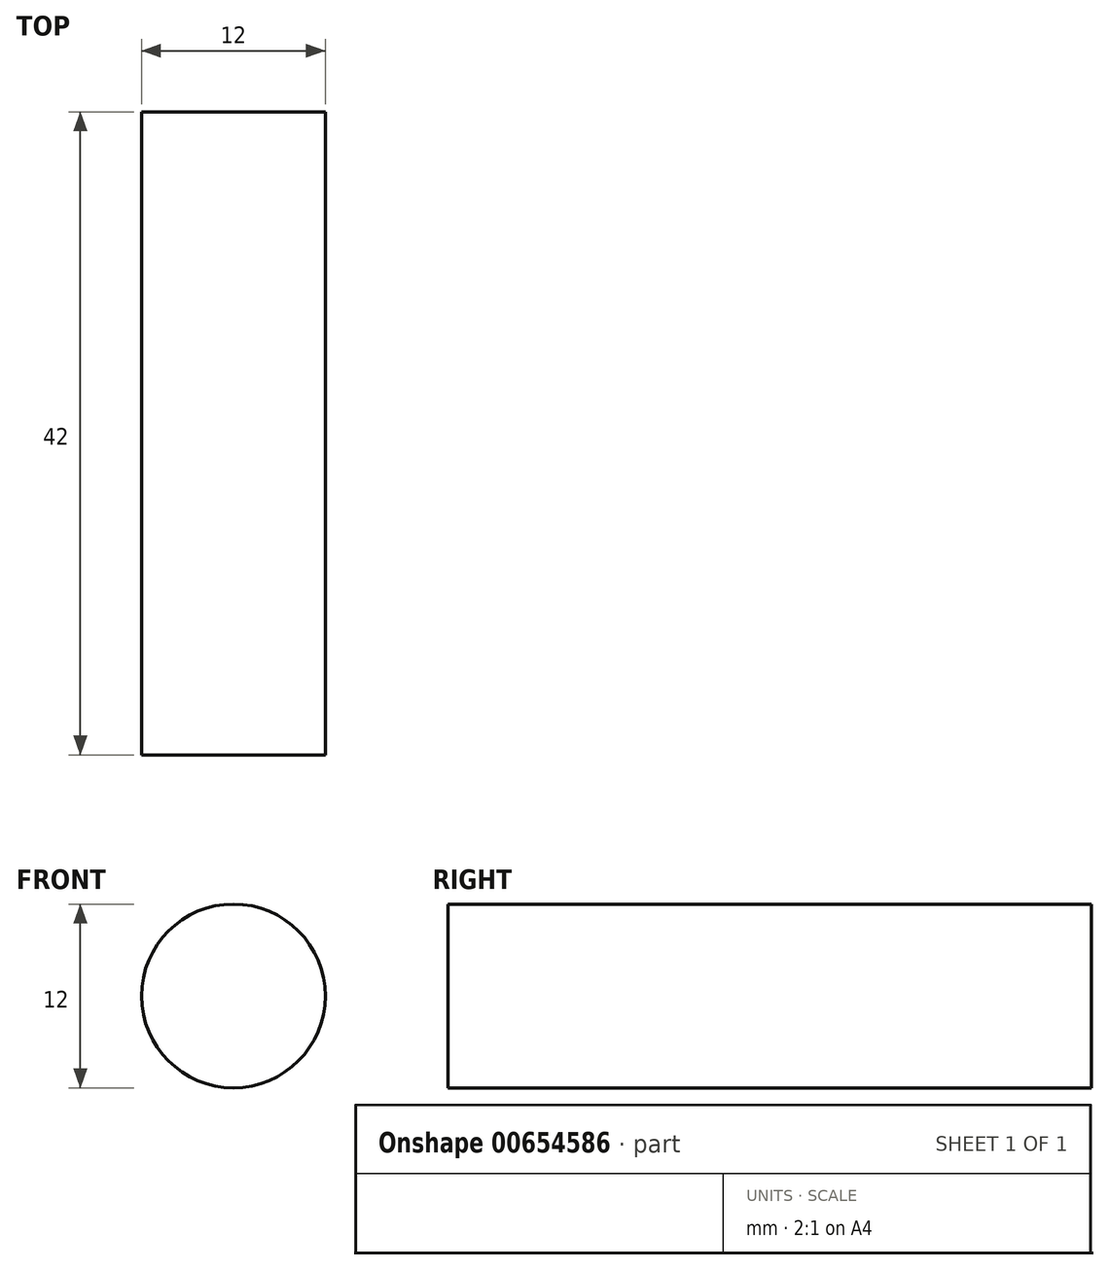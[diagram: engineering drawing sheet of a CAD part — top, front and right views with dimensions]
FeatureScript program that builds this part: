
annotation { "Feature Type Name" : "Feature", "Feature Type Description" : "" }
export const myFeature = defineFeature(function(context is Context, id is Id, definition is map)
    precondition{}
    {
        {
            var Q0;
            Q0=qCreatedBy(makeId("Front.planeOp"),FACE);
            var sketch = newSketch(context, id + "F0", { "sketchPlane" : qUnion([Q0])});
            skCircle(sketch, "E0", {"center": v(0, 0) * mm, "radius": 6 * mm});
            skSolve(sketch);
        }
        {
            var Q0;
            Q0=makeQuery(id+"F0.imprint","IMPRINT",FACE,{"disambiguationData":[TD([[makeQuery(id+"F0.imprint","IMPRINT",EDGE,{"derivedFrom":sQuery(id+"F0.wireOp",EDGE,"E0")}),1.0]])]});
            extrude(context, id + "F1", {"entities" : qUnion([Q0]), "oppositeDirection" : true, "depth" : 42 * mm, "offsetDistance" : 25 * mm});
        }
    });
